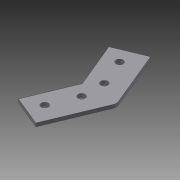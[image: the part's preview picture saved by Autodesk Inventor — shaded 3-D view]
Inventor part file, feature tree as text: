
AUTODESK INVENTOR PART (.ipt)
format: ipt  version: 2015 SP1 (Build 190203100, 203)  size: 105,984 bytes
history: native  units: in
note: dims shown in document units (in); Inventor stores cm internally (conversion verified against a paired STEP export)
features: sheet_metal_op x1, chamfer x1, sketch x1, other x1
ambient origin geometry x8: Origin, YZ Plane, XZ Plane, XY Plane, X Axis, Y Axis, Z Axis, Center Point
bodies: Solid1 (feature_tree)
feature tree (4):
  sheet_metal_op  "Face1"
  chamfer  "Corner Round1"
  sketch  "Sketch1"  dims[d0=1.13in d1=135.0deg d2=2.2in d3=4.0in d4=0.25in d5=1.5748in d7=1.0in d8=0.3937in d10=1.0in d12=0.1464in d13=0.5in d14=0.473in d15=0.5in d16=0.12in d17=0.25in]
  other  "Plate1"
